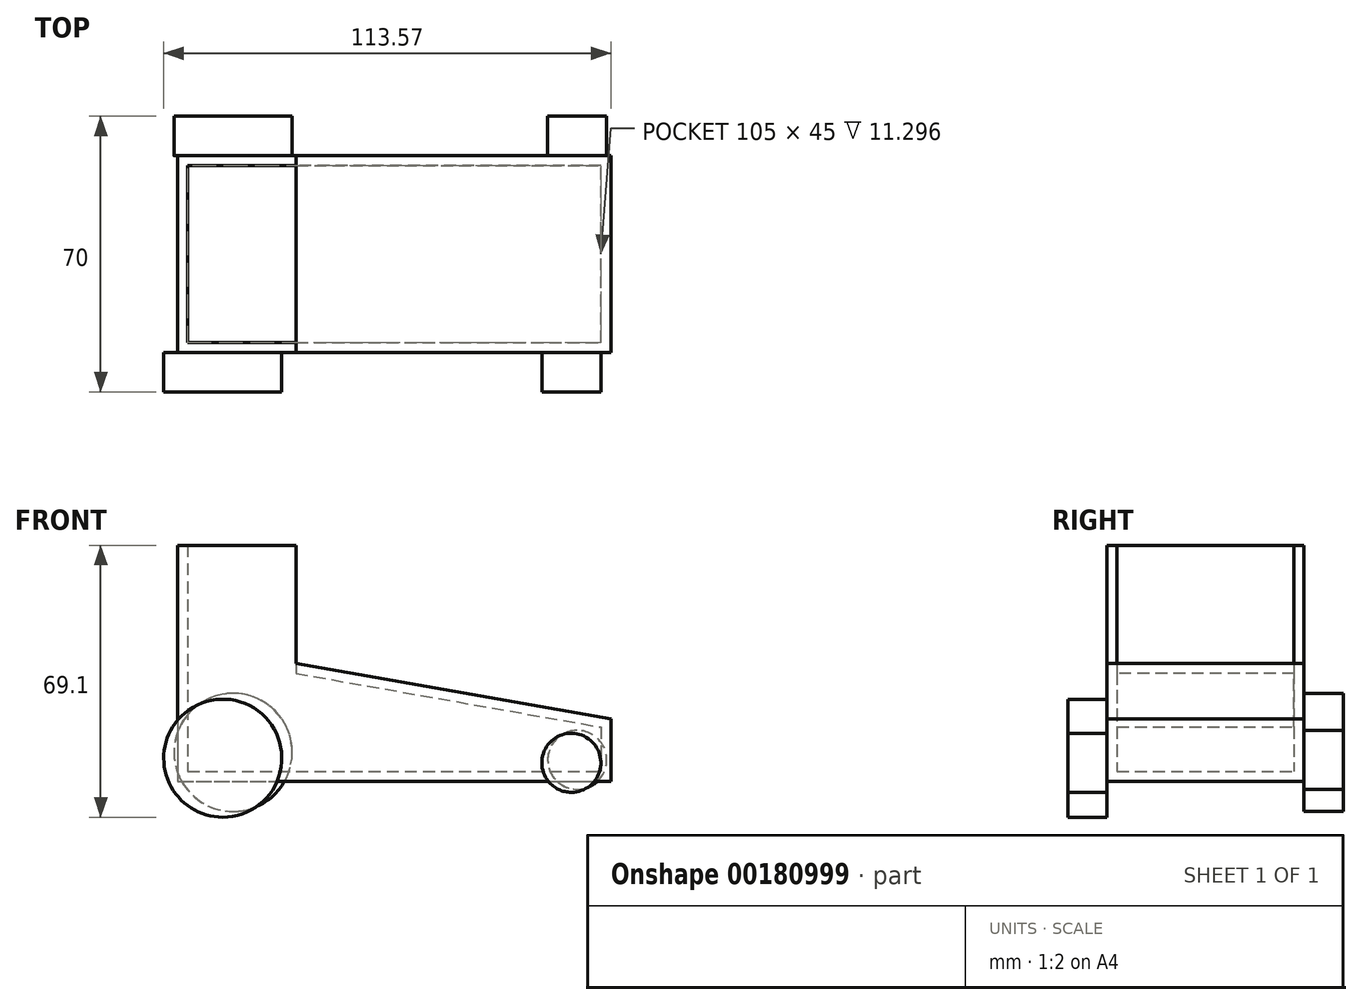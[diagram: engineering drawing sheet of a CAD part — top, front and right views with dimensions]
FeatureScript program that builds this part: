
annotation { "Feature Type Name" : "Feature", "Feature Type Description" : "" }
export const myFeature = defineFeature(function(context is Context, id is Id, definition is map)
    precondition{}
    {
        {
            var Q0;
            Q0=qCreatedBy(makeId("Front.planeOp"),FACE);
            var sketch = newSketch(context, id + "F0", { "sketchPlane" : qUnion([Q0])});
            skLineSegment(sketch, "E0.bottom", {"start": v(-51.72, 38.84) * mm, "end": v(-21.72, 38.84) * mm});
            skLineSegment(sketch, "E0.top", {"start": v(-51.72, -21.16) * mm, "end": v(-21.72, -21.16) * mm});
            skLineSegment(sketch, "E0.left", {"start": v(-51.72, 38.84) * mm, "end": v(-51.72, -21.16) * mm});
            skLineSegment(sketch, "E0.right", {"start": v(-21.72, 38.84) * mm, "end": v(-21.72, -21.16) * mm});
            skSolve(sketch);
        }
        {
            var Q0;
            Q0 = qSketchRegion(id + "F0", true);
            extrude(context, id + "F1", {"entities" : qUnion([Q0]), "depth" : 50 * mm});
        }
        {
            var Q0;
            Q0=makeQuery(id+"F1.opExtrude","SWEPT_FACE",FACE,{"disambiguationData":[OSD([sQuery(id+"F0.wireOp",EDGE,"E0.right")])]});
            var Q1;
            Q1=makeQuery(id+"F1.opExtrude","SWEPT_FACE",FACE,{"disambiguationData":[OSD([sQuery(id+"F0.wireOp",EDGE,"E0.bottom")])]});
            shell(context, id + "F2", {"entities" : qUnion([Q0, Q1]), "thickness" : 2.5 * mm});
        }
        {
            var Q0;
            Q0=makeQuery(id+"F1.opExtrude","SWEPT_FACE",FACE,{"disambiguationData":[OSD([sQuery(id+"F0.wireOp",EDGE,"E0.right")])]});
            var sketch = newSketch(context, id + "F3", { "sketchPlane" : qUnion([Q0])});
            skLineSegment(sketch, "E1.bottom", {"start": v(-50, -21.16) * mm, "end": v(0, -21.16) * mm});
            skLineSegment(sketch, "E1.top", {"start": v(-50, 8.84) * mm, "end": v(0, 8.84) * mm});
            skLineSegment(sketch, "E1.left", {"start": v(-50, -21.16) * mm, "end": v(-50, 8.84) * mm});
            skLineSegment(sketch, "E1.right", {"start": v(0, -21.16) * mm, "end": v(0, 8.84) * mm});
            skSolve(sketch);
        }
        {
            var Q0;
            Q0 = qSketchRegion(id + "F3", true);
            extrude(context, id + "F4", {"entities" : qUnion([Q0]), "operationType" : NewBodyOperationType.ADD, "depth" : 80 * mm});
        }
        {
            var Q0;
            Q0=makeQuery(id+"F4.opExtrude","CAP_EDGE",EDGE,{"disambiguationData":[OSD([sQuery(id+"F3.wireOp",EDGE,"E1.top")])],"isStart":false});
            chamfer(context, id + "F5", {"entities" : qUnion([Q0]), "chamferType" : ChamferType.OFFSET_ANGLE, "width" : 80 * mm, "oppositeDirection" : false, "angle" : 10 * degree, "tangentPropagation" : true});
        }
        {
            var Q0;
            Q0=makeQuery(id+"F4.opExtrude","CAP_FACE",FACE,{"disambiguationData":[OSD([sQuery(id+"F3.wireOp",EDGE,"E1.bottom"),sQuery(id+"F3.wireOp",EDGE,"E1.top"),sQuery(id+"F3.wireOp",EDGE,"E1.left"),sQuery(id+"F3.wireOp",EDGE,"E1.right")])],"isStart":true});
            shell(context, id + "F6", {"entities" : qUnion([Q0]), "thickness" : 2.5 * mm});
        }
        {
            var Q0;
            Q0=makeQuery(id+"F4.boolean.opBoolean","MERGE",FACE,{"derivedFrom":[makeQuery(id+"F1.opExtrude","CAP_FACE",FACE,{"disambiguationData":[OSD([sQuery(id+"F0.wireOp",EDGE,"E0.bottom"),sQuery(id+"F0.wireOp",EDGE,"E0.top"),sQuery(id+"F0.wireOp",EDGE,"E0.left"),sQuery(id+"F0.wireOp",EDGE,"E0.right")])],"isStart":false}),makeQuery(id+"F4.opExtrude","SWEPT_FACE",FACE,{"disambiguationData":[OSD([sQuery(id+"F3.wireOp",EDGE,"E1.left")])]})]});
            var sketch = newSketch(context, id + "F7", { "sketchPlane" : qUnion([Q0])});
            skSolve(sketch);
        }
        {
            var Q0;
            {var subQ4=sQuery(id+"F0.wireOp",EDGE,"E0.bottom");Q0=makeQuery(id+"F7.imprint","IMPRINT",FACE,{"disambiguationData":[TD([[makeQuery(id+"F7.imprint","IMPRINT",EDGE,{"derivedFrom":makeQuery(id+"F1.opExtrude","CAP_EDGE",EDGE,{"disambiguationData":[OSD([subQ4])],"isStart":false})}),-1.0]])]});}
            var sketch = newSketch(context, id + "F8", { "sketchPlane" : qUnion([Q0])});
            skCircle(sketch, "E2", {"center": v(48.26, -16.42) * mm, "radius": 7.5 * mm});
            skSolve(sketch);
        }
        {
            var Q0;
            Q0 = qSketchRegion(id + "F8", true);
            extrude(context, id + "F9", {"entities" : qUnion([Q0]), "operationType" : NewBodyOperationType.ADD, "depth" : 10 * mm});
        }
        {
            var Q0;
            {var subQ4=sQuery(id+"F0.wireOp",EDGE,"E0.bottom");Q0=makeQuery(id+"F7.imprint","IMPRINT",FACE,{"disambiguationData":[TD([[makeQuery(id+"F7.imprint","IMPRINT",EDGE,{"derivedFrom":makeQuery(id+"F1.opExtrude","CAP_EDGE",EDGE,{"disambiguationData":[OSD([subQ4])],"isStart":false})}),-1.0]])]});}
            var sketch = newSketch(context, id + "F10", { "sketchPlane" : qUnion([Q0])});
            skCircle(sketch, "E3", {"center": v(-40.3, -15.26) * mm, "radius": 15 * mm});
            skSolve(sketch);
        }
        {
            var Q0;
            Q0=makeQuery(id+"F4.boolean.opBoolean","MERGE",FACE,{"derivedFrom":[makeQuery(id+"F1.opExtrude","CAP_FACE",FACE,{"disambiguationData":[OSD([sQuery(id+"F0.wireOp",EDGE,"E0.bottom"),sQuery(id+"F0.wireOp",EDGE,"E0.top"),sQuery(id+"F0.wireOp",EDGE,"E0.left"),sQuery(id+"F0.wireOp",EDGE,"E0.right")])],"isStart":true}),makeQuery(id+"F4.opExtrude","SWEPT_FACE",FACE,{"disambiguationData":[OSD([sQuery(id+"F3.wireOp",EDGE,"E1.right")])]})]});
            var sketch = newSketch(context, id + "F11", { "sketchPlane" : qUnion([Q0])});
            skCircle(sketch, "E4", {"center": v(-49.75, -15.68) * mm, "radius": 7.5 * mm});
            skSolve(sketch);
        }
        {
            var Q0;
            Q0 = qSketchRegion(id + "F11", true);
            extrude(context, id + "F12", {"entities" : qUnion([Q0]), "operationType" : NewBodyOperationType.ADD, "depth" : 10 * mm});
        }
        {
            var Q0;
            {var subQ0=sQuery(id+"F10.wireOp",EDGE,"E3");var subQ1=makeQuery(id+"F7.imprint","IMPRINT",EDGE,{"derivedFrom":makeQuery(id+"F1.opExtrude","CAP_EDGE",EDGE,{"disambiguationData":[OSD([sQuery(id+"F0.wireOp",EDGE,"E0.left")])],"isStart":false})});var subQ2=makeQuery(id+"F10.imprint","INTERSECT",VERTEX,{"derivedFrom":[subQ1,subQ0]});Q0=makeQuery(id+"F10.imprint","IMPRINT",FACE,{"disambiguationData":[TD([[makeQuery(id+"F10.imprint","IMPRINT",EDGE,{"disambiguationData":[TD([[subQ2,-1.0]])],"derivedFrom":subQ0}),1.0]])]});}
            var Q1;
            {var subQ0=sQuery(id+"F10.wireOp",EDGE,"E3");var subQ1=makeQuery(id+"F7.imprint","IMPRINT",EDGE,{"derivedFrom":makeQuery(id+"F1.opExtrude","CAP_EDGE",EDGE,{"disambiguationData":[OSD([sQuery(id+"F0.wireOp",EDGE,"E0.left")])],"isStart":false})});var subQ2=makeQuery(id+"F10.imprint","INTERSECT",VERTEX,{"derivedFrom":[subQ1,subQ0]});Q1=makeQuery(id+"F10.imprint","IMPRINT",FACE,{"disambiguationData":[TD([[makeQuery(id+"F10.imprint","IMPRINT",EDGE,{"disambiguationData":[TD([[subQ2,1.0]])],"derivedFrom":subQ0}),1.0]])]});}
            extrude(context, id + "F13", {"entities" : qUnion([Q0, Q1]), "operationType" : NewBodyOperationType.ADD, "depth" : 10 * mm});
        }
        {
            var Q0;
            Q0=qCreatedBy(makeId("Front.planeOp"),FACE);
            var sketch = newSketch(context, id + "F14", { "sketchPlane" : qUnion([Q0])});
            skCircle(sketch, "E5", {"center": v(-37.67, -13.78) * mm, "radius": 15 * mm});
            skSolve(sketch);
        }
        {
            var Q0;
            Q0 = qSketchRegion(id + "F14", true);
            extrude(context, id + "F15", {"entities" : qUnion([Q0]), "operationType" : NewBodyOperationType.ADD, "oppositeDirection" : true, "depth" : 10 * mm});
        }
    });
